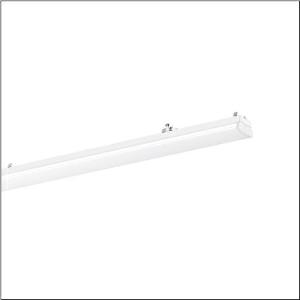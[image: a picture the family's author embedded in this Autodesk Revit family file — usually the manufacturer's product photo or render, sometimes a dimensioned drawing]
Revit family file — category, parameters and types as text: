
# Revit family: licross_r__11_recessed_opal_mo_51tl1ddn425g_3105
name_source: partatom
category: Lighting Fixtures
units: mm (PartAtom-declared; Revit-internal decimal feet)

## family parameters
Cut with Voids When Loaded = No
Host = Face
Light Source = No
Part Type = Normal
Room Calculation Point = No
Round Connector Dimension = Use Diameter
Shared = No

## types (1)
- --- (1 x LED, 2750 lm, 15.7 W, 4000K)
    Apparent Load = 16 VA
    CIE Flux Codes = 44 73 91 87 100
    Color Rendering = 80
    Color Temperature = 4000K
    Default Elevation = 1800 mm
    Description = Licross® 11 recessed opal MO, luminaire insert, of sheet steel, coil coated, white, length: 1.500mm, width: 76mm, height: 87mm, LED rated luminous flux: 2.750lm, light colour: 840, control gear: DALI 2, with plug, 5-pole, with phase selection, mains connection: 220..240V, AC, 50/60Hz, rated input power: 16W, halogen-free wiring, primary optical cover: cover, of PMMA, light emission: direct with ceiling illumination distribution, primary light characteristic: symmetric, protection rating (complete): IP40, insulation class (complete): insulation class I (protective earthing), certification: CE, ENEC, VDE, UKCA, protection symbol: D if used in an environment without relevant dust loads with corresponding accessories, impact resistance: IK06, permissible ambient temperature for indoor applications: -25..+50°C, corresponds to IFS (International Featured Standards) requirements for safety and quality in the food industry, reducing of maximum allowable ambient temperature of 5°C with ceiling mounting, LABS conformity tested according to VDMA 24364:2018-05, packaging unit: 1 piece
    Height = 83 mm
    Lamp = 1 x LED
    Lamp Light Flux = 2750 lm
    Lamp Power = 15.7 W
    Lamp count = 1
    Length = 1500 mm
    Luminous efficacy = 175 lm/W
    Manufacturer = Siteco
    ModVariant = No
    Model = 51TL1DDN425G
    Mounting Place = Ceiling
    Mounting Type = Pendant
    Number of Poles = 1
    OnlyDefault = Yes
    Power Factor = 1
    Product Name = Licross® 11 recessed opal MO
    Product group = luminaire insert
    ProductGroupID = 901
    Protection Class = Protection class I
    Protection Degree = IP 40
    RLX_Detail_Level = 1
    RLX_Emergency_Light_Flux = 0 lm
    RLX_Emergency_Type = 0
    RLX_Emergency_Type_DB = No
    RlxData = <blob elided: 26361 chars, md5=4e1becc7>
    Socket = socket
    Standby Power = 0 W
    System Light Flux = 2750 lm
    System Power = 16 W
    Type Comments = factory setting: luminous flux: 100 % | dim-lin: 254 | 101 mA
    Type Image = l_1313666.jpg
    URL = http://relux.com
    VarID = @adj_045247
    Voltage = 0 V
    Weight = 0.00 kg
    Width = 76 mm

## geometry (parser evidence)
native form markers: Blend x4, Sweep x14
no freeform markers — native parametric forms only
